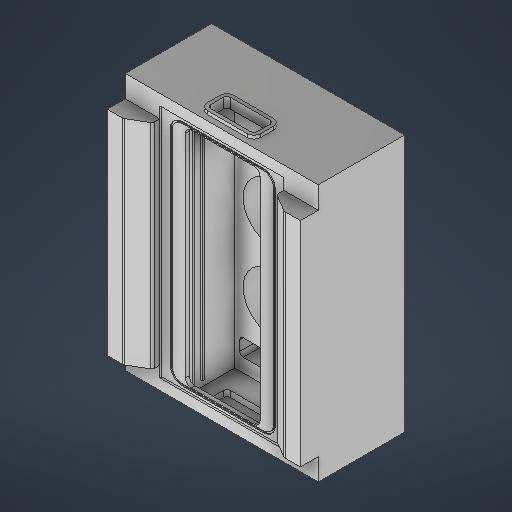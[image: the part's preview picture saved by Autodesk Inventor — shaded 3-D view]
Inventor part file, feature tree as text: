
AUTODESK INVENTOR PART (.ipt)
format: ipt  version: 2025 (Build 290162000, 162)  size: 284,672 bytes
history: native  units: in
note: dims shown in document units (in); Inventor stores cm internally (conversion verified against a paired STEP export)
features: extrude x1, sketch x1
ambient origin geometry x8: Origin, YZ Plane, XZ Plane, XY Plane, X Axis, Y Axis, Z Axis, Center Point
bodies: Solid1 (feature_tree), Body1 (feature_tree)
feature tree (2):
  extrude  "Extrusion1"  Depth=6.6929in
  sketch  "Sketch1"  dims[d0=0.0in d1=0.0in d2=6.6929in d3=6.6929in]
